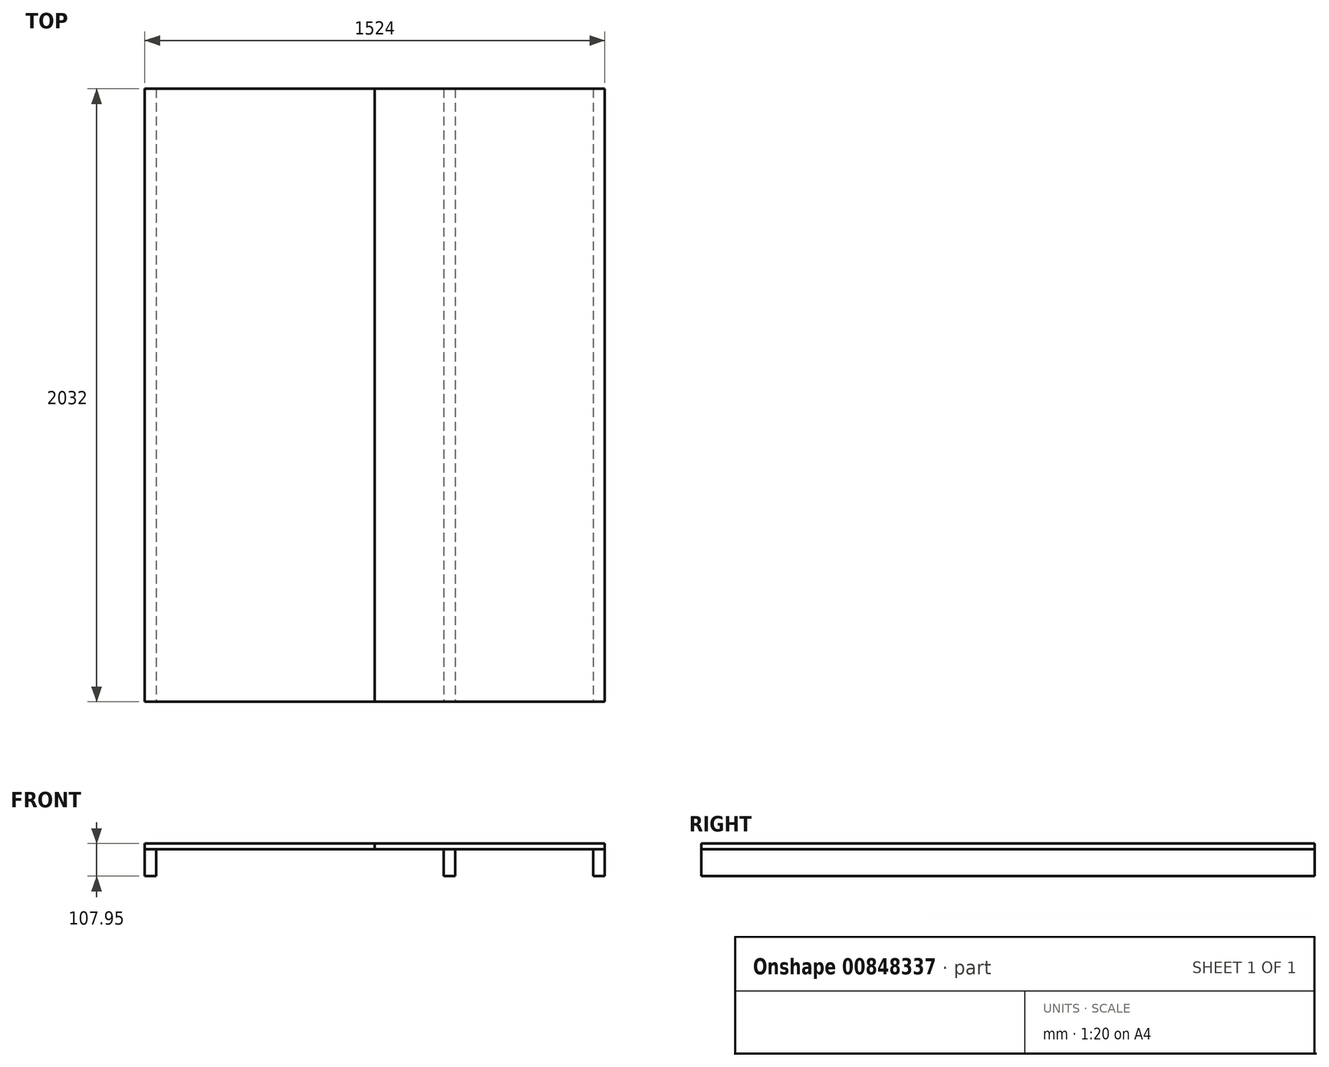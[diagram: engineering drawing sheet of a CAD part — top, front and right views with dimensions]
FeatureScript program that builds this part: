
annotation { "Feature Type Name" : "Feature", "Feature Type Description" : "" }
export const myFeature = defineFeature(function(context is Context, id is Id, definition is map)
    precondition{}
    {
        {
            var Q0;
            Q0=qCreatedBy(makeId("Top.planeOp"),FACE);
            var sketch = newSketch(context, id + "F0", { "sketchPlane" : qUnion([Q0])});
            skLineSegment(sketch, "E0.bottom", {"start": v(-762, 0) * mm, "end": v(762, 0) * mm});
            skLineSegment(sketch, "E0.top", {"start": v(-762, 2032) * mm, "end": v(762, 2032) * mm});
            skLineSegment(sketch, "E0.left", {"start": v(-762, 0) * mm, "end": v(-762, 2032) * mm});
            skLineSegment(sketch, "E0.right", {"start": v(762, 0) * mm, "end": v(762, 2032) * mm});
            skLineSegment(sketch, "E1", {"start": v(0, 2032) * mm, "end": v(0, 0) * mm});
            skSolve(sketch);
        }
        {
            var Q0;
            {var subQ0=sQuery(id+"F0.wireOp",EDGE,"E0.right");Q0=makeQuery(id+"F0.imprint","IMPRINT",FACE,{"disambiguationData":[TD([[makeQuery(id+"F0.imprint","IMPRINT",EDGE,{"derivedFrom":subQ0}),1.0]])]});}
            extrude(context, id + "F1", {"entities" : qUnion([Q0]), "depth" : 19.05 * mm, "offsetDistance" : 25.4 * mm});
        }
        {
            var Q0;
            {var subQ0=sQuery(id+"F0.wireOp",EDGE,"E0.left");Q0=makeQuery(id+"F0.imprint","IMPRINT",FACE,{"disambiguationData":[TD([[makeQuery(id+"F0.imprint","IMPRINT",EDGE,{"derivedFrom":subQ0}),-1.0]])]});}
            extrude(context, id + "F2", {"entities" : qUnion([Q0]), "depth" : 19.05 * mm, "offsetDistance" : 25.4 * mm});
        }
        {
            var Q0;
            Q0=qCreatedBy(makeId("Front.planeOp"),FACE);
            var sketch = newSketch(context, id + "F3", { "sketchPlane" : qUnion([Q0])});
            skLineSegment(sketch, "E2.bottom", {"start": v(762, 0) * mm, "end": v(723.9, 0) * mm});
            skLineSegment(sketch, "E2.top", {"start": v(762, -88.9) * mm, "end": v(723.9, -88.9) * mm});
            skLineSegment(sketch, "E2.left", {"start": v(762, 0) * mm, "end": v(762, -88.9) * mm});
            skLineSegment(sketch, "E2.right", {"start": v(723.9, 0) * mm, "end": v(723.9, -88.9) * mm});
            skSolve(sketch);
        }
        {
            var Q0;
            Q0 = qSketchRegion(id + "F3", true);
            var Q1;
            Q1=makeQuery(id+"F1.opExtrude","SWEPT_FACE",FACE,{"disambiguationData":[OSD([sQuery(id+"F0.wireOp",EDGE,"E0.top")])]});
            extrude(context, id + "F4", {"entities" : qUnion([Q0]), "endBound" : BoundingType.UP_TO_SURFACE, "oppositeDirection" : true, "depth" : 1968.5 * mm, "endBoundEntityFace" : qUnion([Q1]), "offsetDistance" : 25.4 * mm});
        }
        {
            var Q0;
            Q0=makeQuery(id+"F4.opExtrude","SWEPT_BODY",BODY,{"disambiguationData":[OSD([sQuery(id+"F3.wireOp",EDGE,"E2.bottom"),sQuery(id+"F3.wireOp",EDGE,"E2.top"),sQuery(id+"F3.wireOp",EDGE,"E2.left"),sQuery(id+"F3.wireOp",EDGE,"E2.right")])]});
            transform(context, id + "F5", {"entities" : qUnion([Q0]), "transformType" : TransformType.TRANSLATION_3D, "dx" : -1485.9 * mm, "dy" : 0 * mm, "dz" : 0 * mm, "makeCopy" : true});
        }
        {
            var Q0;
            Q0=qCreatedBy(makeId("Right.planeOp"),FACE);
            cPlane(context, id + "F6", {"entities" : qUnion([Q0]), "cplaneType" : CPlaneType.OFFSET, "offset" : 228.6 * mm, "width" : 152.4 * mm, "height" : 152.4 * mm});
        }
        {
            var Q0;
            Q0=qCreatedBy(makeId("Front.planeOp"),FACE);
            var sketch = newSketch(context, id + "F7", { "sketchPlane" : qUnion([Q0])});
            skLineSegment(sketch, "E3.bottom", {"start": v(228.6, 0) * mm, "end": v(266.7, 0) * mm});
            skLineSegment(sketch, "E3.top", {"start": v(228.6, -88.9) * mm, "end": v(266.7, -88.9) * mm});
            skLineSegment(sketch, "E3.left", {"start": v(228.6, 0) * mm, "end": v(228.6, -88.9) * mm});
            skLineSegment(sketch, "E3.right", {"start": v(266.7, 0) * mm, "end": v(266.7, -88.9) * mm});
            skSolve(sketch);
        }
        {
            var Q0;
            Q0 = qSketchRegion(id + "F7", true);
            var Q1;
            Q1=makeQuery(id+"F1.opExtrude","SWEPT_FACE",FACE,{"disambiguationData":[OSD([sQuery(id+"F0.wireOp",EDGE,"E0.top")])]});
            extrude(context, id + "F8", {"entities" : qUnion([Q0]), "endBound" : BoundingType.UP_TO_SURFACE, "oppositeDirection" : true, "depth" : 25.4 * mm, "endBoundEntityFace" : qUnion([Q1]), "offsetDistance" : 25.4 * mm});
        }
    });
